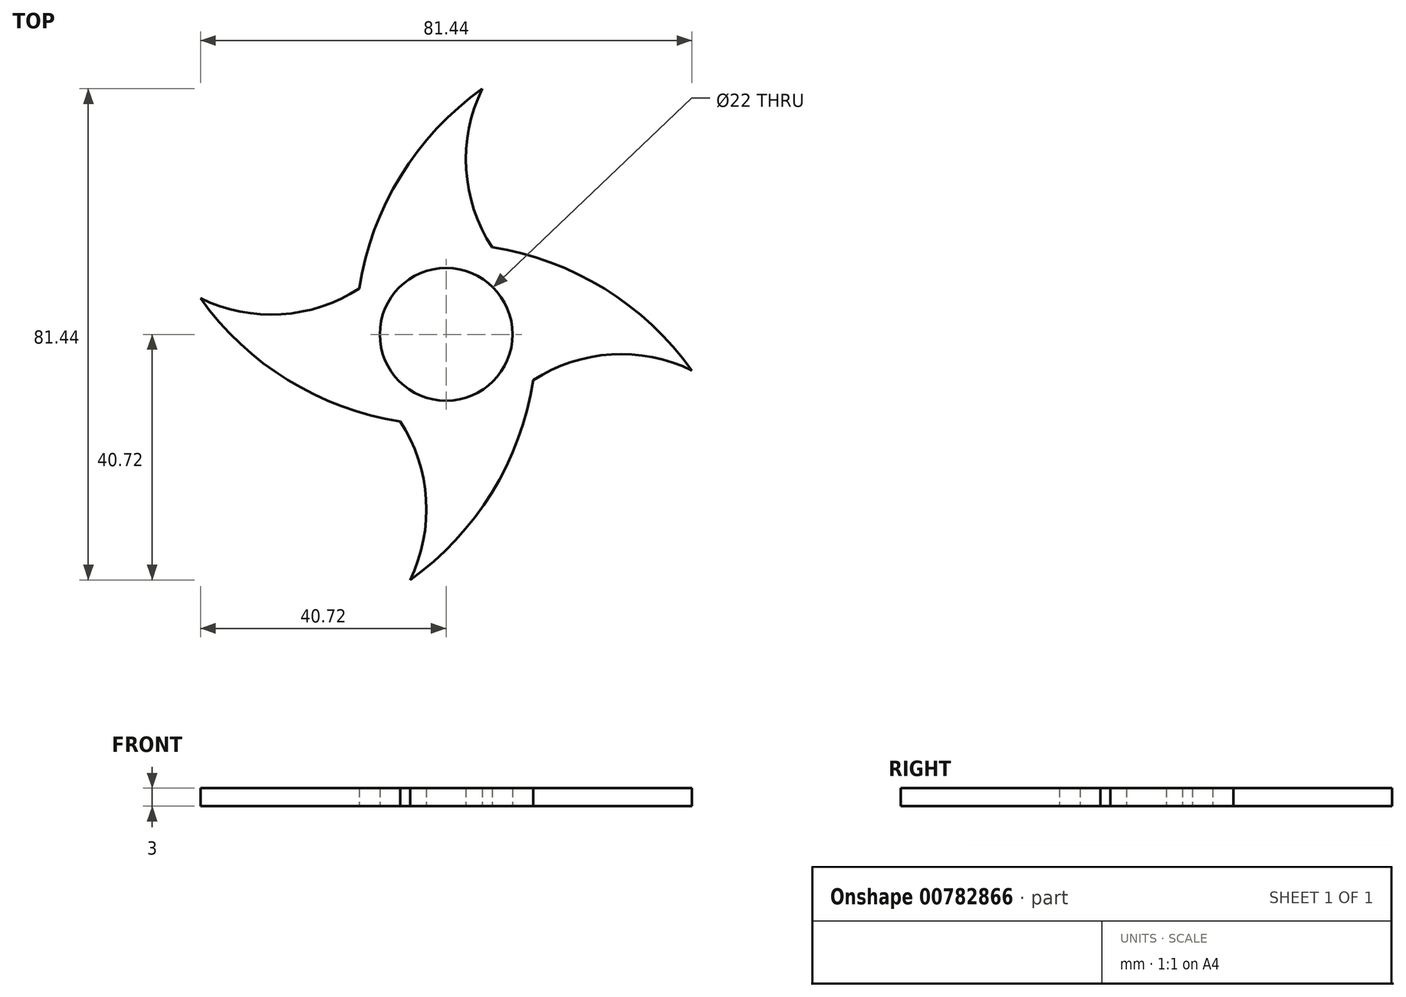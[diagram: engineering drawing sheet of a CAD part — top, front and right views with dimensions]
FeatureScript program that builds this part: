
annotation { "Feature Type Name" : "Feature", "Feature Type Description" : "" }
export const myFeature = defineFeature(function(context is Context, id is Id, definition is map)
    precondition{}
    {
        {
            var Q0;
            Q0=qCreatedBy(makeId("Top.planeOp"),FACE);
            var sketch = newSketch(context, id + "F0", { "sketchPlane" : qUnion([Q0])});
            skCircle(sketch, "E0", {"center": v(0, 0) * mm, "radius": 11 * mm});
            skArc(sketch, "E1", {"start": v(5.98, 40.72) * mm, "mid": v(-7.57, 26.22) * mm, "end": v(-14.42, 7.6) * mm});
            skArc(sketch, "E2", {"start": v(5.98, 40.72) * mm, "mid": v(3.33, 27.35) * mm, "end": v(7.6, 14.42) * mm});
            skArc(sketch, "E3.1.0", {"start": v(-40.72, 5.98) * mm, "mid": v(-27.35, 3.33) * mm, "end": v(-14.42, 7.6) * mm});
            skArc(sketch, "E3.1.1", {"start": v(-40.72, 5.98) * mm, "mid": v(-26.22, -7.57) * mm, "end": v(-7.6, -14.42) * mm});
            skArc(sketch, "E3.2.0", {"start": v(-5.98, -40.72) * mm, "mid": v(-3.33, -27.35) * mm, "end": v(-7.6, -14.42) * mm});
            skArc(sketch, "E3.2.1", {"start": v(-5.98, -40.72) * mm, "mid": v(7.57, -26.22) * mm, "end": v(14.42, -7.6) * mm});
            skArc(sketch, "E3.3.0", {"start": v(40.72, -5.98) * mm, "mid": v(27.35, -3.33) * mm, "end": v(14.42, -7.6) * mm});
            skArc(sketch, "E3.3.1", {"start": v(40.72, -5.98) * mm, "mid": v(26.22, 7.57) * mm, "end": v(7.6, 14.42) * mm});
            skPoint(sketch, "E4.orphan", {"position": v(0, 15) * mm});
            skPoint(sketch, "E5.orphan", {"position": v(15, 0) * mm});
            skPoint(sketch, "E6.orphan", {"position": v(10.78, 10.43) * mm});
            skPoint(sketch, "E7.orphan", {"position": v(10.43, -10.78) * mm});
            skPoint(sketch, "E8.orphan", {"position": v(0, -15) * mm});
            skPoint(sketch, "E9.orphan", {"position": v(-10.78, -10.43) * mm});
            skPoint(sketch, "E10.orphan", {"position": v(-15, 0) * mm});
            skPoint(sketch, "E11.orphan", {"position": v(-10.43, 10.78) * mm});
            skSolve(sketch);
        }
        {
            var Q0;
            Q0 = qSketchRegion(id + "F0", true);
            extrude(context, id + "F1", {"entities" : qUnion([Q0]), "depth" : 3 * mm, "offsetDistance" : 25 * mm});
        }
    });
